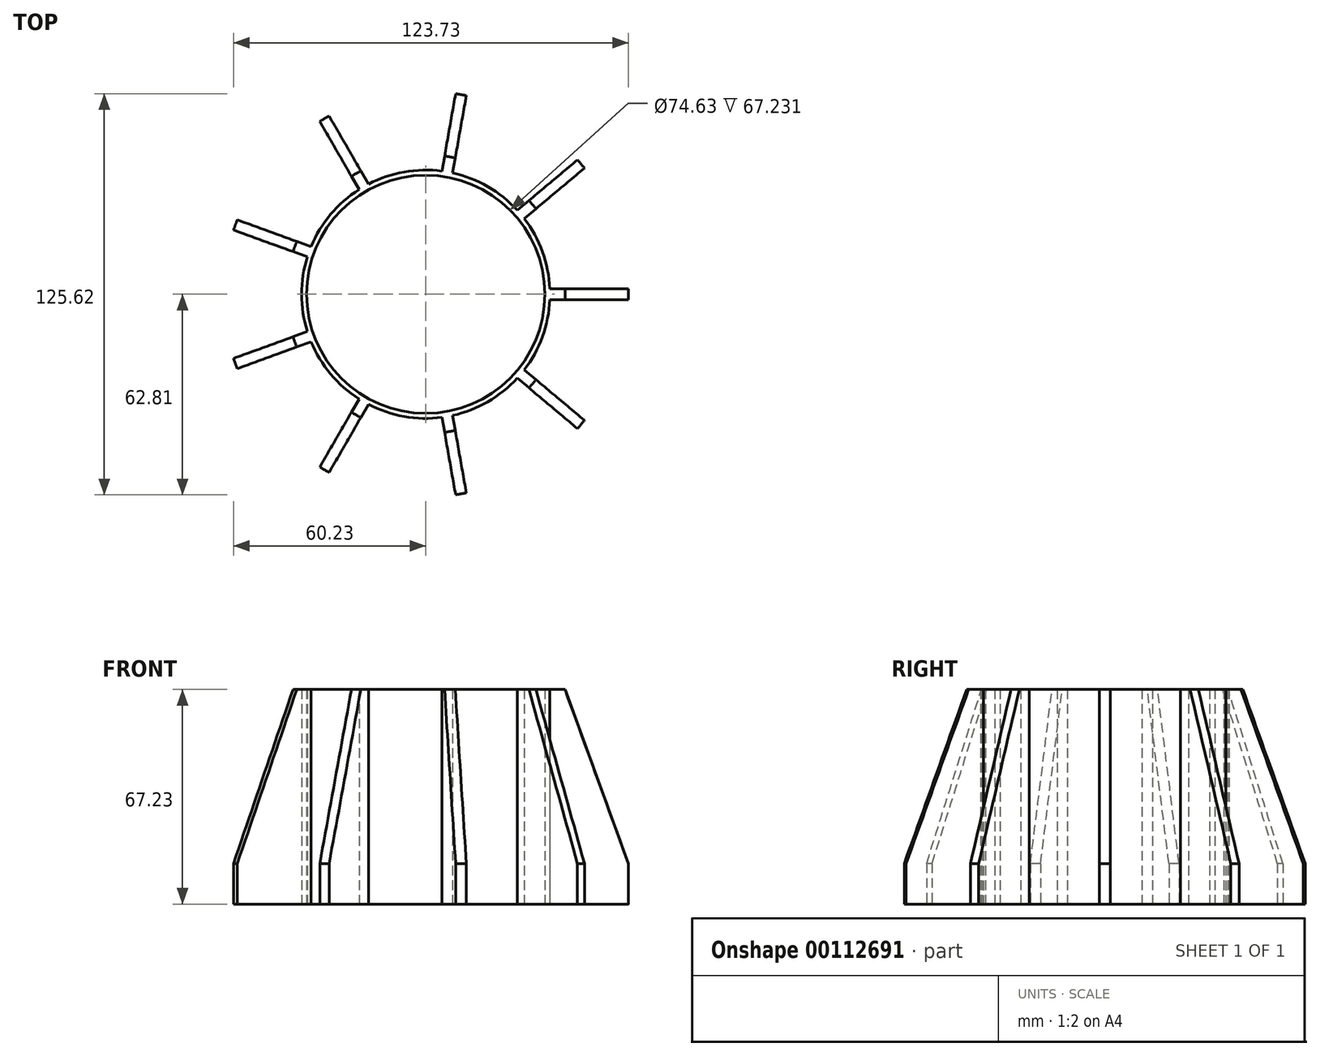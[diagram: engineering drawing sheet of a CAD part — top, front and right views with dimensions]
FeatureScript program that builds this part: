
annotation { "Feature Type Name" : "Feature", "Feature Type Description" : "" }
export const myFeature = defineFeature(function(context is Context, id is Id, definition is map)
    precondition{}
    {
        {
            var Q0;
            Q0=qCreatedBy(makeId("Top.planeOp"),FACE);
            var sketch = newSketch(context, id + "F0", { "sketchPlane" : qUnion([Q0])});
            skCircle(sketch, "E0", {"center": v(0, 0) * mm, "radius": 63.5 * mm});
            skCircle(sketch, "E1", {"center": v(0, 0) * mm, "radius": 37.31 * mm});
            skSolve(sketch);
        }
        {
            var Q0;
            Q0 = qSketchRegion(id + "F0", true);
            extrude(context, id + "F1", {"entities" : qUnion([Q0]), "depth" : 67.23 * mm});
        }
        {
            var Q0;
            Q0=qCreatedBy(makeId("Front.planeOp"),FACE);
            var sketch = newSketch(context, id + "F2", { "sketchPlane" : qUnion([Q0])});
            skLineSegment(sketch, "E2", {"start": v(0, 67.23) * mm, "end": v(43.66, 67.23) * mm});
            skLineSegment(sketch, "E3", {"start": v(43.66, 67.23) * mm, "end": v(63.5, 12.7) * mm});
            skLineSegment(sketch, "E4", {"start": v(63.5, 12.7) * mm, "end": v(63.5, 0) * mm});
            skLineSegment(sketch, "E5", {"start": v(0, 0) * mm, "end": v(63.5, 0) * mm, "construction": true});
            skLineSegment(sketch, "E6.bottom", {"start": v(43.66, 110.9) * mm, "end": v(107.16, 110.9) * mm});
            skLineSegment(sketch, "E6.top", {"start": v(63.5, 0) * mm, "end": v(107.16, 0) * mm});
            skLineSegment(sketch, "E6.left", {"start": v(43.66, 110.9) * mm, "end": v(43.66, 67.23) * mm});
            skLineSegment(sketch, "E6.right", {"start": v(107.16, 110.9) * mm, "end": v(107.16, 0) * mm});
            skSolve(sketch);
        }
        {
            var Q0;
            Q0 = qSketchRegion(id + "F2", true);
            var Q1;
            Q1=makeQuery(id+"F1.opExtrude","CAP_EDGE",EDGE,{"disambiguationData":[OSD([sQuery(id+"F0.wireOp",EDGE,"E0")])],"isStart":false});
            revolve(context, id + "F3", {"operationType" : NewBodyOperationType.REMOVE, "entities" : qUnion([Q0]), "axis" : qUnion([Q1]), "revolveType" : RevolveType.FULL, "oppositeDirection" : true});
        }
        {
            var Q0;
            Q0=makeQuery(id+"F1.opExtrude","CAP_FACE",FACE,{"disambiguationData":[OSD([sQuery(id+"F0.wireOp",EDGE,"E0"),sQuery(id+"F0.wireOp",EDGE,"E1")])],"isStart":true});
            var sketch = newSketch(context, id + "F4", { "sketchPlane" : qUnion([Q0])});
            skArc(sketch, "E7", {"start": v(-37.1, 11.7) * mm, "mid": v(-38.9, 0) * mm, "end": v(-37.1, -11.7) * mm});
            skLineSegment(sketch, "E8", {"start": v(-37.1, -11.7) * mm, "end": v(-60.23, -20.12) * mm});
            skLineSegment(sketch, "E9", {"start": v(-37.1, 11.7) * mm, "end": v(-60.23, 20.12) * mm});
            skArc(sketch, "E10", {"start": v(-60.23, 20.12) * mm, "mid": v(-63.5, 0) * mm, "end": v(-60.23, -20.12) * mm});
            skLineSegment(sketch, "E11", {"start": v(-37.1, 11.7) * mm, "end": v(0, 0) * mm, "construction": true});
            skLineSegment(sketch, "E12", {"start": v(-37.1, -11.7) * mm, "end": v(0, 0) * mm, "construction": true});
            skLineSegment(sketch, "E13", {"start": v(0, 0) * mm, "end": v(-38.9, 0) * mm, "construction": true});
            skLineSegment(sketch, "E14", {"start": v(-48.66, 15.9) * mm, "end": v(-47.5, 19.1) * mm, "construction": true});
            skLineSegment(sketch, "E15", {"start": v(-59.07, 23.3) * mm, "end": v(-35.94, 14.89) * mm, "construction": true});
            skLineSegment(sketch, "E16", {"start": v(-48.08, 17.5) * mm, "end": v(0, 0) * mm, "construction": true});
            skLineSegment(sketch, "E17", {"start": v(0, 0) * mm, "end": v(-35.94, 14.89) * mm, "construction": true});
            skSolve(sketch);
        }
        {
            var Q0;
            Q0 = qSketchRegion(id + "F4", true);
            var Q1;
            Q1=makeQuery(id+"F1.opExtrude","CAP_FACE",FACE,{"disambiguationData":[OSD([sQuery(id+"F0.wireOp",EDGE,"E0"),sQuery(id+"F0.wireOp",EDGE,"E1")])],"isStart":false});
            extrude(context, id + "F5", {"entities" : qUnion([Q0]), "operationType" : NewBodyOperationType.REMOVE, "endBound" : BoundingType.UP_TO_SURFACE, "oppositeDirection" : true, "endBoundEntityFace" : qUnion([Q1]), "depth" : 25.4 * mm});
        }
        {
            var Q0;
            Q0=makeQuery(id+"F5.boolean.opBoolean","COPY",FACE,{"derivedFrom":makeQuery(id+"F5.opExtrude","SWEPT_FACE",FACE,{"disambiguationData":[OSD([sQuery(id+"F4.wireOp",EDGE,"E8")])]})});
            var Q1;
            Q1=makeQuery(id+"F5.boolean.opBoolean","COPY",FACE,{"derivedFrom":makeQuery(id+"F5.opExtrude","SWEPT_FACE",FACE,{"disambiguationData":[OSD([sQuery(id+"F4.wireOp",EDGE,"E7")])]})});
            var Q2;
            Q2=makeQuery(id+"F5.boolean.opBoolean","COPY",FACE,{"derivedFrom":makeQuery(id+"F5.opExtrude","SWEPT_FACE",FACE,{"disambiguationData":[OSD([sQuery(id+"F4.wireOp",EDGE,"E9")])]})});
            var Q3;
            Q3=makeQuery(id+"F1.opExtrude","SWEPT_FACE",FACE,{"disambiguationData":[OSD([sQuery(id+"F0.wireOp",EDGE,"E0")])]});
            circularPattern(context, id + "F6", {"patternType" : PatternType.FACE, "faces" : qUnion([Q0, Q1, Q2]), "axis" : qUnion([Q3]), "angle" : 40 * degree, "instanceCount" : 9});
        }
    });
